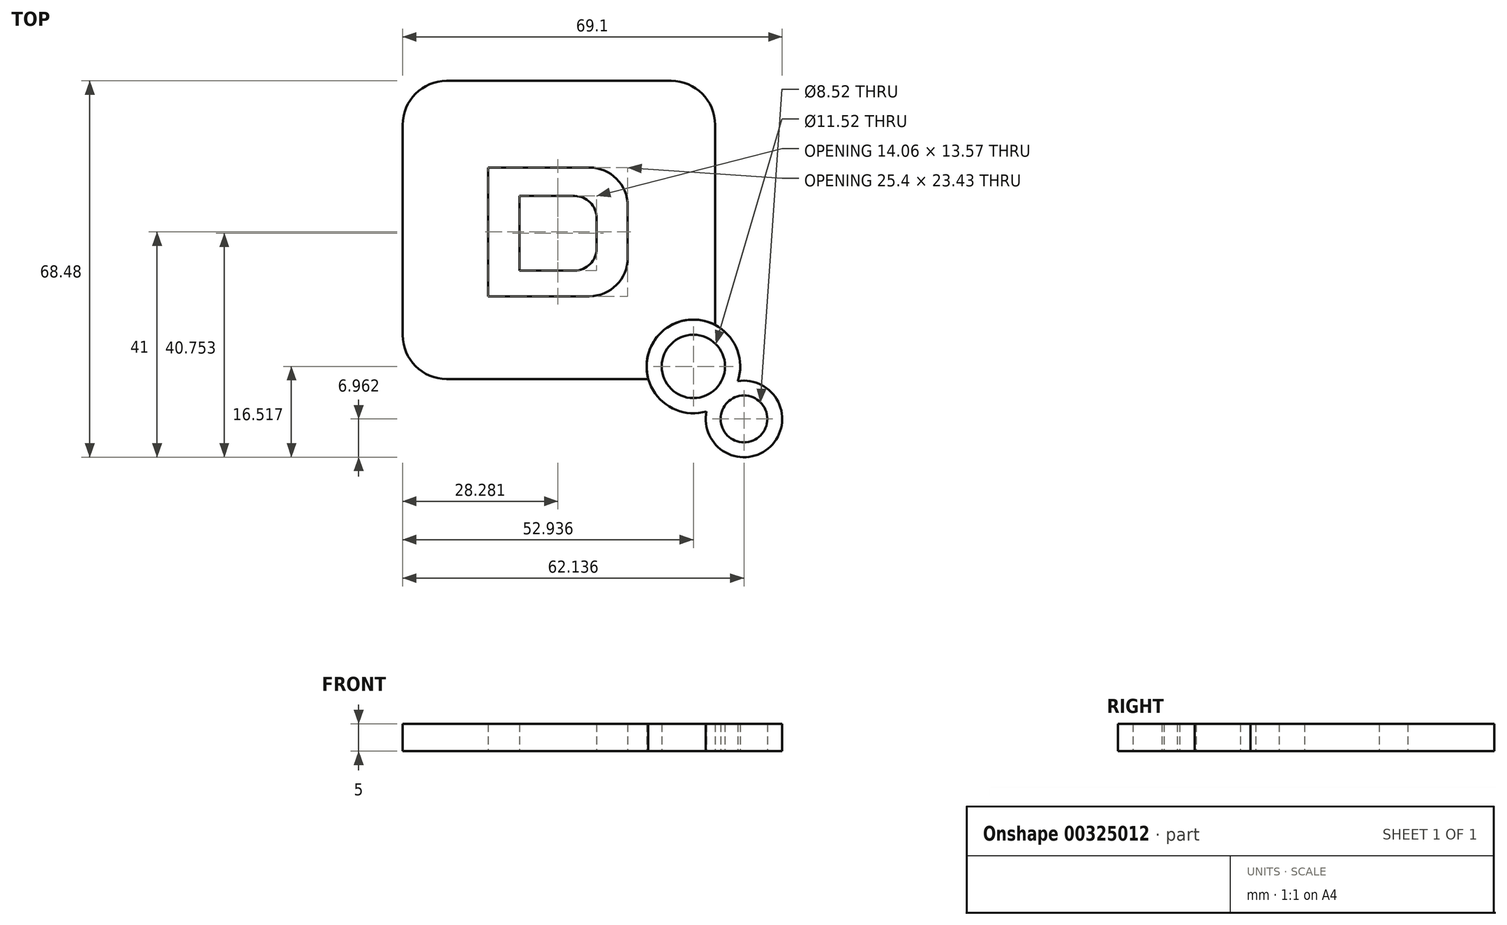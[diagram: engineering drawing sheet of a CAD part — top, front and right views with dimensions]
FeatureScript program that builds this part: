
annotation { "Feature Type Name" : "Feature", "Feature Type Description" : "" }
export const myFeature = defineFeature(function(context is Context, id is Id, definition is map)
    precondition{}
    {
        {
            var Q0;
            Q0=qCreatedBy(makeId("Top.planeOp"),FACE);
            var sketch = newSketch(context, id + "F0", { "sketchPlane" : qUnion([Q0])});
            skLineSegment(sketch, "E0.bottom", {"start": v(-20.44, 27.13) * mm, "end": v(20.44, 27.13) * mm});
            skLineSegment(sketch, "E0.top", {"start": v(-20.44, -27.13) * mm, "end": v(16.29, -27.13) * mm});
            skLineSegment(sketch, "E0.left", {"start": v(-28.44, 19.13) * mm, "end": v(-28.44, -19.13) * mm});
            skLineSegment(sketch, "E0.right", {"start": v(28.44, 19.13) * mm, "end": v(28.44, -17.28) * mm});
            skPoint(sketch, "E0.middle", {"position": v(0, 0) * mm});
            skPoint(sketch, "E1.visualSharp", {"position": v(-28.44, 27.13) * mm});
            skArc(sketch, "E1.filletArc", {"start": v(-20.44, 27.13) * mm, "mid": v(-26.1, 24.79) * mm, "end": v(-28.44, 19.13) * mm});
            skPoint(sketch, "E2.visualSharp", {"position": v(28.44, 27.13) * mm});
            skArc(sketch, "E2.filletArc", {"start": v(28.44, 19.13) * mm, "mid": v(26.1, 24.79) * mm, "end": v(20.44, 27.13) * mm});
            skPoint(sketch, "E3.visualSharp", {"position": v(-28.44, -27.13) * mm});
            skArc(sketch, "E3.filletArc", {"start": v(-28.44, -19.13) * mm, "mid": v(-26.1, -24.79) * mm, "end": v(-20.44, -27.13) * mm});
            skArc(sketch, "E4", {"start": v(28.44, -17.28) * mm, "mid": v(19.13, -18.21) * mm, "end": v(16.29, -27.13) * mm});
            skPoint(sketch, "E5.orphan", {"position": v(28.44, -27.13) * mm});
            skCircle(sketch, "E6", {"center": v(24.5, -24.83) * mm, "radius": 5.76 * mm});
            skCircle(sketch, "E7", {"center": v(33.7, -34.39) * mm, "radius": 4.26 * mm});
            skArc(sketch, "E8", {"start": v(32.59, -27.51) * mm, "mid": v(18.58, -18.7) * mm, "end": v(26.87, -33.02) * mm});
            skArc(sketch, "E9", {"start": v(26.87, -33.02) * mm, "mid": v(38.53, -39.4) * mm, "end": v(32.59, -27.51) * mm});
            skLineSegment(sketch, "E10", {"start": v(-12.86, 11.37) * mm, "end": v(-12.86, -12.07) * mm});
            skLineSegment(sketch, "E11", {"start": v(-12.86, 11.37) * mm, "end": v(5.54, 11.37) * mm});
            skLineSegment(sketch, "E12", {"start": v(12.54, 4.37) * mm, "end": v(12.54, -5.07) * mm});
            skLineSegment(sketch, "E13", {"start": v(5.54, -12.07) * mm, "end": v(-12.86, -12.07) * mm});
            skLineSegment(sketch, "E14", {"start": v(-7.19, 6.19) * mm, "end": v(-7.19, -7.38) * mm});
            skLineSegment(sketch, "E15", {"start": v(-7.19, -7.38) * mm, "end": v(2.87, -7.38) * mm});
            skLineSegment(sketch, "E16", {"start": v(6.87, -3.38) * mm, "end": v(6.87, 2.19) * mm});
            skLineSegment(sketch, "E17", {"start": v(2.87, 6.19) * mm, "end": v(-7.19, 6.19) * mm});
            skPoint(sketch, "E18.orphan", {"position": v(-7.19, 6.68) * mm});
            skPoint(sketch, "E19.visualSharp", {"position": v(12.54, 11.37) * mm});
            skArc(sketch, "E19.filletArc", {"start": v(12.54, 4.37) * mm, "mid": v(10.5, 9.32) * mm, "end": v(5.54, 11.37) * mm});
            skPoint(sketch, "E20.visualSharp", {"position": v(12.54, -12.07) * mm});
            skArc(sketch, "E20.filletArc", {"start": v(5.54, -12.07) * mm, "mid": v(10.5, -10.02) * mm, "end": v(12.54, -5.07) * mm});
            skPoint(sketch, "E21.visualSharp", {"position": v(6.87, -7.38) * mm});
            skArc(sketch, "E21.filletArc", {"start": v(2.87, -7.38) * mm, "mid": v(5.7, -6.2) * mm, "end": v(6.87, -3.38) * mm});
            skPoint(sketch, "E22.visualSharp", {"position": v(6.87, 6.19) * mm});
            skArc(sketch, "E22.filletArc", {"start": v(6.87, 2.19) * mm, "mid": v(5.7, 5.01) * mm, "end": v(2.87, 6.19) * mm});
            skSolve(sketch);
        }
        {
            var Q0;
            Q0=makeQuery(id+"F0.imprint","IMPRINT",FACE,{"disambiguationData":[TD([[makeQuery(id+"F0.imprint","IMPRINT",EDGE,{"derivedFrom":sQuery(id+"F0.wireOp",EDGE,"E0.bottom")}),-1.0]])]});
            var Q1;
            Q1=makeQuery(id+"F0.imprint","IMPRINT",FACE,{"disambiguationData":[TD([[makeQuery(id+"F0.imprint","IMPRINT",EDGE,{"derivedFrom":sQuery(id+"F0.wireOp",EDGE,"E14")}),1.0]])]});
            var Q2;
            Q2=makeQuery(id+"F0.imprint","IMPRINT",FACE,{"disambiguationData":[TD([[makeQuery(id+"F0.imprint","IMPRINT",EDGE,{"derivedFrom":sQuery(id+"F0.wireOp",EDGE,"E6")}),1.0]])]});
            var Q3;
            Q3=makeQuery(id+"F0.imprint","IMPRINT",FACE,{"disambiguationData":[TD([[makeQuery(id+"F0.imprint","IMPRINT",EDGE,{"derivedFrom":sQuery(id+"F0.wireOp",EDGE,"E7")}),1.0]])]});
            extrude(context, id + "F1", {"entities" : qUnion([Q0, Q1, Q2, Q3]), "depth" : 5 * mm});
        }
        {
            var Q0;
            Q0=makeQuery(id+"F0.imprint","IMPRINT",FACE,{"disambiguationData":[TD([[makeQuery(id+"F0.imprint","IMPRINT",EDGE,{"derivedFrom":sQuery(id+"F0.wireOp",EDGE,"E10")}),1.0]])]});
            var Q1;
            Q1=makeQuery(id+"F0.imprint","IMPRINT",FACE,{"disambiguationData":[TD([[makeQuery(id+"F0.imprint","IMPRINT",EDGE,{"derivedFrom":sQuery(id+"F0.wireOp",EDGE,"E6")}),-1.0]])]});
            extrude(context, id + "F2", {"entities" : qUnion([Q0, Q1]), "depth" : 5 * mm});
        }
        {
            var Q0;
            Q0=makeQuery(id+"F1.opExtrude","SWEPT_BODY",BODY,{"disambiguationData":[OSD([sQuery(id+"F0.wireOp",EDGE,"E7")])]});
            deleteBodies(context, id + "F3", {"entities" : qUnion([Q0])});
        }
    });
